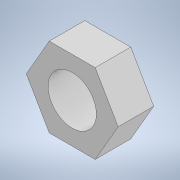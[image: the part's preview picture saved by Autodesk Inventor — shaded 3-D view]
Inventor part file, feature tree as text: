
AUTODESK INVENTOR PART (.ipt)
format: ipt  version: 2022 (Build 260153000, 153)  size: 105,472 bytes
history: native  units: mm
features: extrude x1, sketch x1
ambient origin geometry x8: Origin, YZ Plane, XZ Plane, XY Plane, X Axis, Y Axis, Z Axis, Center Point
bodies: Solid1 (feature_tree)
feature tree (2):
  extrude  "Extrusion1"  Depth=3.02mm TaperAngle=360.0deg
  sketch  "Sketch1"  dims[d0=3.9mm d1=60.0mm d3=360.0deg d5=4.1mm d6=3.02mm d7=0.0mm]
